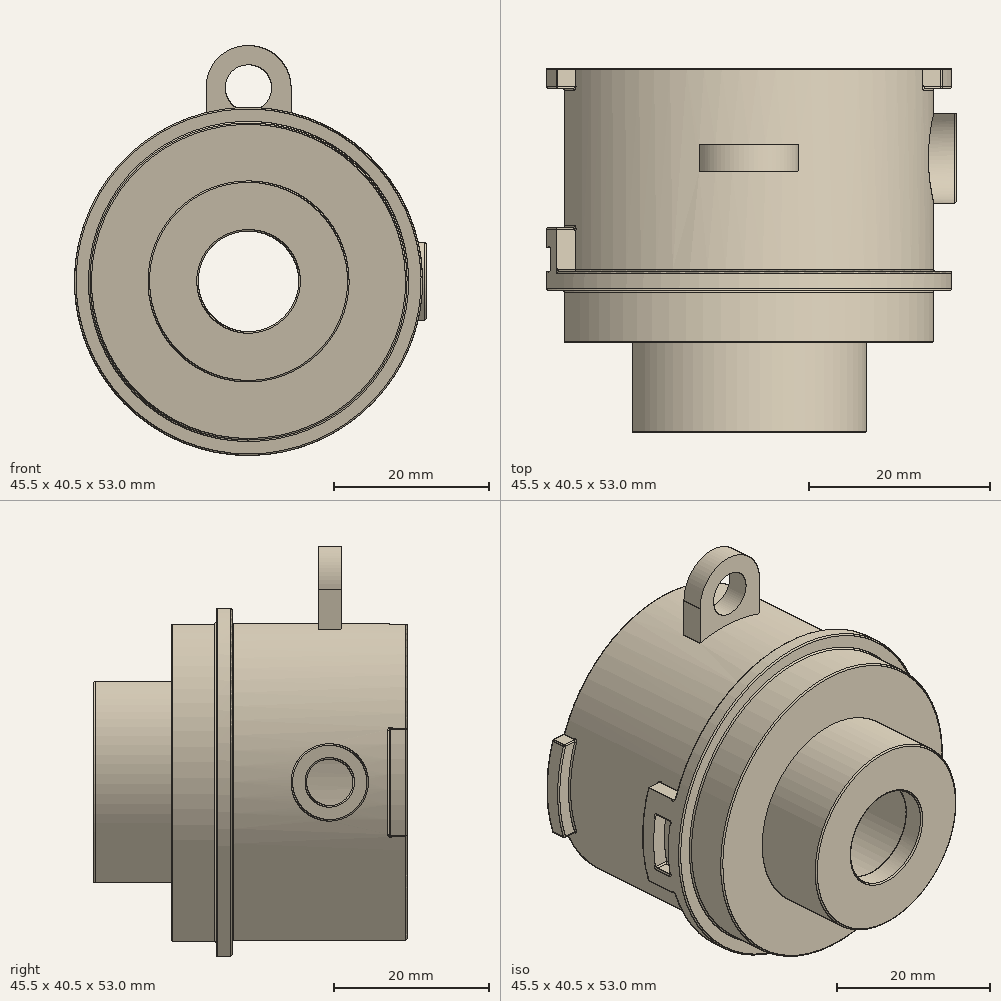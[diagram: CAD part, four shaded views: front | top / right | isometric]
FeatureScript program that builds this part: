
annotation { "Feature Type Name" : "Feature", "Feature Type Description" : "" }
export const myFeature = defineFeature(function(context is Context, id is Id, definition is map)
    precondition{}
    {
        {
            var Q0;
            Q0=qCreatedBy(makeId("Front.planeOp"),FACE);
            var sketch = newSketch(context, id + "F0", { "sketchPlane" : qUnion([Q0])});
            skCircle(sketch, "E0", {"center": v(0, 0) * mm, "radius": 18.45 * mm});
            skCircle(sketch, "E1", {"center": v(0, 0) * mm, "radius": 20.5 * mm});
            skLineSegment(sketch, "E2.bottom", {"start": v(-19.27, 7) * mm, "end": v(-21.38, 7) * mm});
            skLineSegment(sketch, "E3.MirrorCS", {"start": v(19.27, 7) * mm, "end": v(21.38, 7) * mm});
            skLineSegment(sketch, "E4.MirrorCS", {"start": v(-19.27, -7) * mm, "end": v(-21.38, -7) * mm});
            skLineSegment(sketch, "E5.MirrorCS", {"start": v(19.27, -7) * mm, "end": v(21.38, -7) * mm});
            skArc(sketch, "E6", {"start": v(21.38, -7) * mm, "mid": v(22.5, 0) * mm, "end": v(21.38, 7) * mm});
            skArc(sketch, "E7.trimOffspring", {"start": v(-21.38, 7) * mm, "mid": v(-22.5, 0) * mm, "end": v(-21.38, -7) * mm});
            skSolve(sketch);
        }
        {
            var Q0;
            Q0=makeQuery(id+"F0.imprint","IMPRINT",FACE,{"disambiguationData":[TD([[makeQuery(id+"F0.imprint","IMPRINT",EDGE,{"derivedFrom":sQuery(id+"F0.wireOp",EDGE,"E0")}),-1.0]])]});
            extrude(context, id + "F1", {"entities" : qUnion([Q0]), "depth" : 27.5 * mm});
        }
        {
            var Q0;
            {var subQ0=sQuery(id+"F0.wireOp",EDGE,"E2.bottom");Q0=makeQuery(id+"F0.imprint","IMPRINT",FACE,{"disambiguationData":[TD([[makeQuery(id+"F0.imprint","IMPRINT",EDGE,{"derivedFrom":subQ0}),1.0]])]});}
            var Q1;
            {var subQ0=sQuery(id+"F0.wireOp",EDGE,"E3.MirrorCS");Q1=makeQuery(id+"F0.imprint","IMPRINT",FACE,{"disambiguationData":[TD([[makeQuery(id+"F0.imprint","IMPRINT",EDGE,{"derivedFrom":subQ0}),-1.0]])]});}
            extrude(context, id + "F2", {"entities" : qUnion([Q0, Q1]), "operationType" : NewBodyOperationType.ADD, "depth" : 2.3 * mm});
        }
        {
            var Q0;
            Q0=qCreatedBy(makeId("Front.planeOp"),FACE);
            cPlane(context, id + "F3", {"entities" : qUnion([Q0]), "cplaneType" : CPlaneType.OFFSET, "offset" : 2.1 * mm, "width" : 150 * mm, "height" : 150 * mm});
        }
        {
            var Q0;
            Q0=qCreatedBy(id+"F3.planeOp",FACE);
            var sketch = newSketch(context, id + "F4", { "sketchPlane" : qUnion([Q0])});
            skCircle(sketch, "E8", {"center": v(0, 0) * mm, "radius": 19.5 * mm});
            skLineSegment(sketch, "E9", {"start": v(0, 0) * mm, "end": v(-19.34, 2.5) * mm});
            skLineSegment(sketch, "E10", {"start": v(0, 0) * mm, "end": v(-19.34, -2.5) * mm});
            skLineSegment(sketch, "E11", {"start": v(0, 0) * mm, "end": v(-17.3, -9) * mm});
            skSolve(sketch);
        }
        {
            var Q0;
            {var subQ0=sQuery(id+"F4.wireOp",EDGE,"E9");Q0=makeQuery(id+"F4.imprint","IMPRINT",FACE,{"disambiguationData":[TD([[makeQuery(id+"F4.imprint","IMPRINT",EDGE,{"derivedFrom":subQ0}),1.0]])]});}
            var Q1;
            {var subQ0=sQuery(id+"F4.wireOp",EDGE,"E10");Q1=makeQuery(id+"F4.imprint","IMPRINT",FACE,{"disambiguationData":[TD([[makeQuery(id+"F4.imprint","IMPRINT",EDGE,{"derivedFrom":subQ0}),1.0]])]});}
            extrude(context, id + "F5", {"entities" : qUnion([Q0, Q1]), "operationType" : NewBodyOperationType.REMOVE, "depth" : 1.8 * mm});
        }
        {
            var Q0;
            {var subQ0=sQuery(id+"F4.wireOp",EDGE,"E10");Q0=makeQuery(id+"F4.imprint","IMPRINT",FACE,{"disambiguationData":[TD([[makeQuery(id+"F4.imprint","IMPRINT",EDGE,{"derivedFrom":subQ0}),1.0]])]});}
            extrude(context, id + "F6", {"entities" : qUnion([Q0]), "operationType" : NewBodyOperationType.REMOVE, "oppositeDirection" : true, "depth" : 25 * mm});
        }
        {
            var Q0;
            Q0=qCreatedBy(makeId("Front.planeOp"),FACE);
            var sketch = newSketch(context, id + "F7", { "sketchPlane" : qUnion([Q0])});
            skLineSegment(sketch, "E12.bottom", {"start": v(-1.65, 19.45) * mm, "end": v(1.65, 19.45) * mm});
            skLineSegment(sketch, "E12.top", {"start": v(-1.65, -19.45) * mm, "end": v(1.65, -19.45) * mm});
            skLineSegment(sketch, "E12.left", {"start": v(-1.65, 19.45) * mm, "end": v(-1.65, -19.45) * mm});
            skLineSegment(sketch, "E12.right", {"start": v(1.65, 19.45) * mm, "end": v(1.65, -19.45) * mm});
            skSolve(sketch);
        }
        {
            var Q0;
            Q0=makeQuery(id+"F7.imprint","IMPRINT",FACE,{"disambiguationData":[TD([[makeQuery(id+"F7.imprint","IMPRINT",EDGE,{"derivedFrom":sQuery(id+"F7.wireOp",EDGE,"E12.bottom")}),-1.0]])]});
            extrude(context, id + "F8", {"entities" : qUnion([Q0]), "operationType" : NewBodyOperationType.REMOVE, "depth" : 6.4 * mm});
        }
        {
            var Q0;
            Q0=makeQuery(id+"F8.boolean.opBoolean","INTERSECT",EDGE,{"disambiguationData":[OD(0.0)],"derivedFrom":[makeQuery(id+"F1.opExtrude","SWEPT_FACE",FACE,{"disambiguationData":[OSD([sQuery(id+"F0.wireOp",EDGE,"E0")])]}),makeQuery(id+"F8.opExtrude","SWEPT_FACE",FACE,{"disambiguationData":[OSD([sQuery(id+"F7.wireOp",EDGE,"E12.left")])]})]});
            var Q1;
            Q1=makeQuery(id+"F8.boolean.opBoolean","INTERSECT",EDGE,{"disambiguationData":[OD(0.0)],"derivedFrom":[makeQuery(id+"F1.opExtrude","SWEPT_FACE",FACE,{"disambiguationData":[OSD([sQuery(id+"F0.wireOp",EDGE,"E0")])]}),makeQuery(id+"F8.opExtrude","SWEPT_FACE",FACE,{"disambiguationData":[OSD([sQuery(id+"F7.wireOp",EDGE,"E12.right")])]})]});
            var Q2;
            Q2=makeQuery(id+"F8.boolean.opBoolean","INTERSECT",EDGE,{"disambiguationData":[OD(1.0)],"derivedFrom":[makeQuery(id+"F1.opExtrude","SWEPT_FACE",FACE,{"disambiguationData":[OSD([sQuery(id+"F0.wireOp",EDGE,"E0")])]}),makeQuery(id+"F8.opExtrude","SWEPT_FACE",FACE,{"disambiguationData":[OSD([sQuery(id+"F7.wireOp",EDGE,"E12.left")])]})]});
            var Q3;
            Q3=makeQuery(id+"F8.boolean.opBoolean","INTERSECT",EDGE,{"disambiguationData":[OD(1.0)],"derivedFrom":[makeQuery(id+"F1.opExtrude","SWEPT_FACE",FACE,{"disambiguationData":[OSD([sQuery(id+"F0.wireOp",EDGE,"E0")])]}),makeQuery(id+"F8.opExtrude","SWEPT_FACE",FACE,{"disambiguationData":[OSD([sQuery(id+"F7.wireOp",EDGE,"E12.right")])]})]});
            chamfer(context, id + "F9", {"entities" : qUnion([Q0, Q1, Q2, Q3]), "width" : 1 * mm, "tangentPropagation" : true});
        }
        {
            var Q0;
            Q0=qCreatedBy(makeId("Front.planeOp"),FACE);
            cPlane(context, id + "F10", {"entities" : qUnion([Q0]), "cplaneType" : CPlaneType.OFFSET, "offset" : 22.6 * mm, "width" : 150 * mm, "height" : 150 * mm});
        }
        {
            var Q0;
            Q0=qCreatedBy(id+"F10.planeOp",FACE);
            var sketch = newSketch(context, id + "F11", { "sketchPlane" : qUnion([Q0])});
            skCircle(sketch, "E13", {"center": v(0, 0) * mm, "radius": 22.5 * mm});
            skArc(sketch, "E14.0.0", {"start": v(-19.27, -7) * mm, "mid": v(-20.5, 0) * mm, "end": v(-19.27, 7) * mm});
            skLineSegment(sketch, "E14.0.1", {"start": v(-19.27, 7) * mm, "end": v(-21.38, 7) * mm});
            skArc(sketch, "E14.0.2", {"start": v(-21.38, 7) * mm, "mid": v(-22.5, 0) * mm, "end": v(-21.38, -7) * mm});
            skLineSegment(sketch, "E14.0.3", {"start": v(-21.38, -7) * mm, "end": v(-19.27, -7) * mm});
            skLineSegment(sketch, "E15.0.0", {"start": v(21.38, 7) * mm, "end": v(19.27, 7) * mm});
            skArc(sketch, "E15.0.1", {"start": v(19.27, 7) * mm, "mid": v(20.5, 0) * mm, "end": v(19.27, -7) * mm});
            skLineSegment(sketch, "E15.0.2", {"start": v(19.27, -7) * mm, "end": v(21.38, -7) * mm});
            skArc(sketch, "E15.0.3", {"start": v(21.38, -7) * mm, "mid": v(22.5, 0) * mm, "end": v(21.38, 7) * mm});
            skLineSegment(sketch, "E16", {"start": v(-20.1, 4) * mm, "end": v(-22.14, 4) * mm});
            skLineSegment(sketch, "E17", {"start": v(-20.1, -4) * mm, "end": v(-22.14, -4) * mm});
            skCircle(sketch, "E18", {"center": v(0, 0) * mm, "radius": 20.5 * mm});
            skSolve(sketch);
        }
        {
            var Q0;
            {var subQ0=sQuery(id+"F11.wireOp",EDGE,"E14.0.1");Q0=makeQuery(id+"F11.imprint","IMPRINT",FACE,{"disambiguationData":[TD([[makeQuery(id+"F11.imprint","IMPRINT",EDGE,{"derivedFrom":subQ0}),1.0]])]});}
            var Q1;
            {var subQ0=sQuery(id+"F11.wireOp",EDGE,"E16");Q1=makeQuery(id+"F11.imprint","IMPRINT",FACE,{"disambiguationData":[TD([[makeQuery(id+"F11.imprint","IMPRINT",EDGE,{"derivedFrom":subQ0}),1.0]])]});}
            var Q2;
            {var subQ0=sQuery(id+"F11.wireOp",EDGE,"E14.0.3");Q2=makeQuery(id+"F11.imprint","IMPRINT",FACE,{"disambiguationData":[TD([[makeQuery(id+"F11.imprint","IMPRINT",EDGE,{"derivedFrom":subQ0}),1.0]])]});}
            extrude(context, id + "F12", {"entities" : qUnion([Q0, Q1, Q2]), "operationType" : NewBodyOperationType.ADD, "oppositeDirection" : true, "depth" : 4.9 * mm, "hasSecondDirection" : true, "secondDirectionOppositeDirection" : false, "secondDirectionDepth" : 2.1 * mm});
        }
        {
            var Q0;
            {var subQ0=sQuery(id+"F11.wireOp",EDGE,"E16");Q0=makeQuery(id+"F11.imprint","IMPRINT",FACE,{"disambiguationData":[TD([[makeQuery(id+"F11.imprint","IMPRINT",EDGE,{"derivedFrom":subQ0}),1.0]])]});}
            extrude(context, id + "F13", {"entities" : qUnion([Q0]), "operationType" : NewBodyOperationType.REMOVE, "oppositeDirection" : true, "depth" : 2.7 * mm});
        }
        {
            var Q0;
            {var subQ0=sQuery(id+"F11.wireOp",EDGE,"E14.0.3");Q0=makeQuery(id+"F11.imprint","IMPRINT",FACE,{"disambiguationData":[TD([[makeQuery(id+"F11.imprint","IMPRINT",EDGE,{"derivedFrom":subQ0}),-1.0]])]});}
            var Q1;
            {var subQ0=sQuery(id+"F11.wireOp",EDGE,"E14.0.1");Q1=makeQuery(id+"F11.imprint","IMPRINT",FACE,{"disambiguationData":[TD([[makeQuery(id+"F11.imprint","IMPRINT",EDGE,{"derivedFrom":subQ0}),-1.0]])]});}
            var Q2;
            {var subQ0=sQuery(id+"F11.wireOp",EDGE,"E15.0.0");Q2=makeQuery(id+"F11.imprint","IMPRINT",FACE,{"disambiguationData":[TD([[makeQuery(id+"F11.imprint","IMPRINT",EDGE,{"derivedFrom":subQ0}),1.0]])]});}
            extrude(context, id + "F14", {"entities" : qUnion([Q0, Q1, Q2]), "operationType" : NewBodyOperationType.ADD, "depth" : 2.1 * mm});
        }
        {
            var Q0;
            Q0=makeQuery(id+"F13.boolean.opBoolean","COPY",FACE,{"derivedFrom":makeQuery(id+"F13.opExtrude","SWEPT_FACE",FACE,{"disambiguationData":[OSD([sQuery(id+"F11.wireOp",EDGE,"E16")])]})});
            var Q1;
            Q1=makeQuery(id+"F13.boolean.opBoolean","COPY",FACE,{"derivedFrom":makeQuery(id+"F13.opExtrude","SWEPT_FACE",FACE,{"disambiguationData":[OSD([sQuery(id+"F11.wireOp",EDGE,"E17")])]})});
            var Q2;
            Q2=makeQuery(id+"F12.opExtrude","CAP_FACE",FACE,{"disambiguationData":[OSD([sQuery(id+"F11.wireOp",EDGE,"E13"),sQuery(id+"F11.wireOp",EDGE,"E14.0.1"),sQuery(id+"F11.wireOp",EDGE,"E14.0.3"),sQuery(id+"F11.wireOp",EDGE,"E18")])],"isStart":false});
            var Q3;
            {var subQ0=sQuery(id+"F11.wireOp",EDGE,"E13");var subQ1=sQuery(id+"F11.wireOp",EDGE,"E14.0.3");var subQ2=sQuery(id+"F11.wireOp",EDGE,"E14.0.1");Q3=makeQuery(id+"F14.boolean.opBoolean","SPLIT",FACE,{"disambiguationData":[TD([makeQuery(id+"F12.opExtrude","SWEPT_FACE",FACE,{"disambiguationData":[OSD([subQ1])]})])],"derivedFrom":makeQuery(id+"F14.opExtrude","CAP_FACE",FACE,{"disambiguationData":[OSD([subQ0,subQ2,subQ1,sQuery(id+"F11.wireOp",EDGE,"E18")])],"isStart":true})});}
            var Q4;
            {var subQ0=sQuery(id+"F11.wireOp",EDGE,"E13");var subQ1=sQuery(id+"F11.wireOp",EDGE,"E14.0.1");var subQ2=sQuery(id+"F11.wireOp",EDGE,"E14.0.3");Q4=makeQuery(id+"F14.boolean.opBoolean","SPLIT",FACE,{"disambiguationData":[TD([makeQuery(id+"F12.opExtrude","SWEPT_FACE",FACE,{"disambiguationData":[OSD([subQ1])]})])],"derivedFrom":makeQuery(id+"F14.opExtrude","CAP_FACE",FACE,{"disambiguationData":[OSD([subQ0,subQ1,subQ2,sQuery(id+"F11.wireOp",EDGE,"E18")])],"isStart":true})});}
            var Q5;
            Q5=makeQuery(id+"FDiJdH3o1XdmGiN_1.1.F12.opExtrude","CAP_FACE",FACE,{"disambiguationData":[OSD([sQuery(id+"F11.wireOp",EDGE,"E13"),sQuery(id+"F11.wireOp",EDGE,"E14.0.1"),sQuery(id+"F11.wireOp",EDGE,"E14.0.3"),sQuery(id+"F11.wireOp",EDGE,"E18")])],"isStart":false});
            var Q6;
            Q6=makeQuery(id+"FDiJdH3o1XdmGiN_1.1.F13.boolean.opBoolean","COPY",FACE,{"derivedFrom":makeQuery(id+"FDiJdH3o1XdmGiN_1.1.F13.opExtrude","SWEPT_FACE",FACE,{"disambiguationData":[OSD([sQuery(id+"F11.wireOp",EDGE,"E17")])]})});
            var Q7;
            Q7=makeQuery(id+"FDiJdH3o1XdmGiN_1.1.F13.boolean.opBoolean","COPY",FACE,{"derivedFrom":makeQuery(id+"FDiJdH3o1XdmGiN_1.1.F13.opExtrude","SWEPT_FACE",FACE,{"disambiguationData":[OSD([sQuery(id+"F11.wireOp",EDGE,"E16")])]})});
            fillet(context, id + "F15", {"entities" : qUnion([Q0, Q1, Q2, Q3, Q4, Q5, Q6, Q7]), "radius" : 0.2 * mm, "tangentPropagation" : true, "allowEdgeOverflow" : false});
        }
        {
            var Q0;
            {var subQ0=sQuery(id+"F11.wireOp",EDGE,"E18");var subQ1=sQuery(id+"F11.wireOp",EDGE,"E14.0.3");var subQ2=sQuery(id+"F11.wireOp",EDGE,"E14.0.1");var subQ3=sQuery(id+"F11.wireOp",EDGE,"E13");Q0=makeQuery(id+"F14.boolean.opBoolean","MERGE",FACE,{"derivedFrom":[makeQuery(id+"F12.opExtrude","CAP_FACE",FACE,{"disambiguationData":[OSD([subQ3,subQ2,subQ1,subQ0])],"isStart":true}),makeQuery(id+"FDiJdH3o1XdmGiN_1.1.F12.opExtrude","CAP_FACE",FACE,{"disambiguationData":[OSD([subQ3,subQ2,subQ1,subQ0])],"isStart":true}),makeQuery(id+"F14.opExtrude","CAP_FACE",FACE,{"disambiguationData":[OSD([subQ3,subQ2,subQ1,subQ0])],"isStart":false})]});}
            var Q1;
            Q1=makeQuery(id+"F2.opExtrude","CAP_FACE",FACE,{"disambiguationData":[OSD([sQuery(id+"F0.wireOp",EDGE,"E1"),sQuery(id+"F0.wireOp",EDGE,"E2.bottom"),sQuery(id+"F0.wireOp",EDGE,"E4.MirrorCS"),sQuery(id+"F0.wireOp",EDGE,"E7.trimOffspring")])],"isStart":false});
            var Q2;
            Q2=makeQuery(id+"F2.opExtrude","CAP_FACE",FACE,{"disambiguationData":[OSD([sQuery(id+"F0.wireOp",EDGE,"E1"),sQuery(id+"F0.wireOp",EDGE,"E3.MirrorCS"),sQuery(id+"F0.wireOp",EDGE,"E5.MirrorCS"),sQuery(id+"F0.wireOp",EDGE,"E6")])],"isStart":false});
            var Q3;
            {var subQ0=sQuery(id+"F0.wireOp",EDGE,"E1");Q3=makeQuery(id+"F2.boolean.opBoolean","MERGE",FACE,{"derivedFrom":[makeQuery(id+"F1.opExtrude","CAP_FACE",FACE,{"disambiguationData":[OSD([sQuery(id+"F0.wireOp",EDGE,"E0"),subQ0])],"isStart":true}),makeQuery(id+"F2.opExtrude","CAP_FACE",FACE,{"disambiguationData":[OSD([subQ0,sQuery(id+"F0.wireOp",EDGE,"E2.bottom"),sQuery(id+"F0.wireOp",EDGE,"E4.MirrorCS"),sQuery(id+"F0.wireOp",EDGE,"E7.trimOffspring")])],"isStart":true}),makeQuery(id+"F2.opExtrude","CAP_FACE",FACE,{"disambiguationData":[OSD([subQ0,sQuery(id+"F0.wireOp",EDGE,"E3.MirrorCS"),sQuery(id+"F0.wireOp",EDGE,"E5.MirrorCS"),sQuery(id+"F0.wireOp",EDGE,"E6")])],"isStart":true})]});}
            var Q4;
            Q4=makeQuery(id+"F2.opExtrude","SWEPT_FACE",FACE,{"disambiguationData":[OSD([sQuery(id+"F0.wireOp",EDGE,"E6")])]});
            var Q5;
            Q5=makeQuery(id+"F2.opExtrude","SWEPT_FACE",FACE,{"disambiguationData":[OSD([sQuery(id+"F0.wireOp",EDGE,"E7.trimOffspring")])]});
            fillet(context, id + "F16", {"entities" : qUnion([Q0, Q1, Q2, Q3, Q4, Q5]), "radius" : 0.2 * mm, "tangentPropagation" : true, "allowEdgeOverflow" : false});
        }
        {
            var Q0;
            Q0=makeQuery(id+"F1.opExtrude","CAP_FACE",FACE,{"disambiguationData":[OSD([sQuery(id+"F0.wireOp",EDGE,"E0"),sQuery(id+"F0.wireOp",EDGE,"E1")])],"isStart":false});
            var sketch = newSketch(context, id + "F17", { "sketchPlane" : qUnion([Q0])});
            skCircle(sketch, "E19.0", {"center": v(0, 0) * mm, "radius": 18.45 * mm});
            skCircle(sketch, "E20", {"center": v(0, 0) * mm, "radius": 9 * mm});
            skSolve(sketch);
        }
        {
            var Q0;
            Q0=makeQuery(id+"F17.imprint","IMPRINT",FACE,{"disambiguationData":[TD([[makeQuery(id+"F17.imprint","IMPRINT",EDGE,{"derivedFrom":sQuery(id+"F17.wireOp",EDGE,"E19.0")}),1.0]])]});
            var Q1;
            Q1=makeQuery(id+"F17.imprint","IMPRINT",FACE,{"disambiguationData":[TD([[makeQuery(id+"F17.imprint","IMPRINT",EDGE,{"derivedFrom":sQuery(id+"F17.wireOp",EDGE,"E19.0")}),-1.0]])]});
            extrude(context, id + "F18", {"entities" : qUnion([Q0, Q1]), "operationType" : NewBodyOperationType.ADD, "depth" : 3 * mm});
        }
        {
            var Q0;
            Q0=qCreatedBy(makeId("Top.planeOp"),FACE);
            var sketch = newSketch(context, id + "F19", { "sketchPlane" : qUnion([Q0])});
            skLineSegment(sketch, "E21", {"start": v(13, -40.5) * mm, "end": v(13, -30.5) * mm});
            skLineSegment(sketch, "E22", {"start": v(13, -30.5) * mm, "end": v(9, -30.5) * mm});
            skLineSegment(sketch, "E23.top", {"start": v(9, -37.5) * mm, "end": v(6.5, -37.5) * mm});
            skLineSegment(sketch, "E23.right", {"start": v(6.5, -40.5) * mm, "end": v(6.5, -37.5) * mm});
            skLineSegment(sketch, "E24", {"start": v(9, -30.5) * mm, "end": v(9, -37.5) * mm});
            skLineSegment(sketch, "E25", {"start": v(6.5, -40.5) * mm, "end": v(13, -40.5) * mm});
            skLineSegment(sketch, "E26", {"start": v(0, 0) * mm, "end": v(0, -50) * mm, "construction": true});
            skSolve(sketch);
        }
        {
            var Q0;
            Q0=makeQuery(id+"F19.imprint","IMPRINT",FACE,{"disambiguationData":[TD([[makeQuery(id+"F19.imprint","IMPRINT",EDGE,{"derivedFrom":sQuery(id+"F19.wireOp",EDGE,"E21")}),1.0]])]});
            var Q1;
            Q1=sQuery(id+"F19.wireOp",EDGE,"E26");
            revolve(context, id + "F20", {"operationType" : NewBodyOperationType.ADD, "entities" : qUnion([Q0]), "axis" : qUnion([Q1]), "revolveType" : RevolveType.FULL});
        }
        {
            var Q0;
            Q0=makeQuery(id+"F18.opExtrude","CAP_EDGE",EDGE,{"disambiguationData":[OSD([sQuery(id+"F0.wireOp",EDGE,"E1")])],"isStart":false});
            var Q1;
            Q1=makeQuery(id+"F1.opExtrude","CAP_EDGE",EDGE,{"disambiguationData":[OSD([sQuery(id+"F0.wireOp",EDGE,"E0")])],"isStart":false});
            var Q2;
            Q2=makeQuery(id+"F20.opRevolve","SWEPT_EDGE",EDGE,{"disambiguationData":[OSD([sQuery(id+"F19.wireOp",EDGE,"TMA1aJ2l-3Chm-zUbr-5o9L-zpnb6GAkEytc"),sQuery(id+"F19.wireOp",EDGE,"E21")])]});
            var Q3;
            Q3=makeQuery(id+"F20.opRevolve","SWEPT_EDGE",EDGE,{"disambiguationData":[OSD([sQuery(id+"F19.wireOp",EDGE,"E23.bottom"),sQuery(id+"F19.wireOp",EDGE,"E23.right")])]});
            var Q4;
            Q4=makeQuery(id+"F20.opRevolve","SWEPT_FACE",FACE,{"disambiguationData":[OSD([sQuery(id+"F19.wireOp",EDGE,"E23.top")])]});
            var Q5;
            Q5=makeQuery(id+"F18.opExtrude","CAP_EDGE",EDGE,{"disambiguationData":[OSD([sQuery(id+"F17.wireOp",EDGE,"E20")])],"isStart":true});
            fillet(context, id + "F21", {"entities" : qUnion([Q0, Q1, Q2, Q3, Q4, Q5]), "radius" : 0.2 * mm, "tangentPropagation" : true, "allowEdgeOverflow" : false});
        }
        {
            var Q0;
            Q0=qCreatedBy(makeId("Front.planeOp"),FACE);
            cPlane(context, id + "F22", {"entities" : qUnion([Q0]), "cplaneType" : CPlaneType.OFFSET, "offset" : 10 * mm, "width" : 150 * mm, "height" : 150 * mm});
        }
        {
            var Q0;
            Q0=qCreatedBy(id+"F22.planeOp",FACE);
            var sketch = newSketch(context, id + "F23", { "sketchPlane" : qUnion([Q0])});
            skCircle(sketch, "E27", {"center": v(0, 25) * mm, "radius": 3 * mm});
            skArc(sketch, "E28", {"start": v(5.5, 25) * mm, "mid": v(0, 30.5) * mm, "end": v(-5.5, 25) * mm});
            skLineSegment(sketch, "E29", {"start": v(5.5, 25) * mm, "end": v(5.5, 19) * mm});
            skLineSegment(sketch, "E30", {"start": v(5.5, 19) * mm, "end": v(-5.5, 19) * mm});
            skLineSegment(sketch, "E31", {"start": v(-5.5, 19) * mm, "end": v(-5.5, 25) * mm});
            skSolve(sketch);
        }
        {
            var Q0;
            Q0 = qSketchRegion(id + "F23", true);
            extrude(context, id + "F24", {"entities" : qUnion([Q0]), "operationType" : NewBodyOperationType.ADD, "endBound" : BoundingType.SYMMETRIC, "depth" : 3 * mm});
        }
        {
            var Q0;
            Q0=qCreatedBy(makeId("Right.planeOp"),FACE);
            cPlane(context, id + "F25", {"entities" : qUnion([Q0]), "cplaneType" : CPlaneType.OFFSET, "offset" : 23 * mm, "width" : 150 * mm, "height" : 150 * mm});
        }
        {
            var Q0;
            Q0=qCreatedBy(id+"F25.planeOp",FACE);
            var sketch = newSketch(context, id + "F26", { "sketchPlane" : qUnion([Q0])});
            skCircle(sketch, "E32", {"center": v(-10, 0) * mm, "radius": 3 * mm});
            skCircle(sketch, "E33", {"center": v(-10, 0) * mm, "radius": 5 * mm});
            skSolve(sketch);
        }
        {
            var Q0;
            Q0=makeQuery(id+"F26.imprint","IMPRINT",FACE,{"disambiguationData":[TD([[makeQuery(id+"F26.imprint","IMPRINT",EDGE,{"derivedFrom":sQuery(id+"F26.wireOp",EDGE,"E32")}),1.0]])]});
            var Q1;
            Q1=makeQuery(id+"F1.opExtrude","SWEPT_FACE",FACE,{"disambiguationData":[OSD([sQuery(id+"F0.wireOp",EDGE,"E0")])]});
            extrude(context, id + "F27", {"entities" : qUnion([Q0]), "operationType" : NewBodyOperationType.REMOVE, "endBound" : BoundingType.UP_TO_SURFACE, "oppositeDirection" : true, "endBoundEntityFace" : qUnion([Q1]), "depth" : 50 * mm});
        }
        {
            var Q0;
            Q0=makeQuery(id+"F26.imprint","IMPRINT",FACE,{"disambiguationData":[TD([[makeQuery(id+"F26.imprint","IMPRINT",EDGE,{"derivedFrom":sQuery(id+"F26.wireOp",EDGE,"E32")}),-1.0]])]});
            extrude(context, id + "F28", {"entities" : qUnion([Q0]), "operationType" : NewBodyOperationType.ADD, "endBound" : BoundingType.UP_TO_NEXT, "oppositeDirection" : true, "depth" : 25 * mm});
        }
        {
            var Q0;
            Q0=makeQuery(id+"F24.opExtrude","CAP_FACE",FACE,{"disambiguationData":[OSD([sQuery(id+"F23.wireOp",EDGE,"GQkDEcLr-gr8e-p2JM-y6pI-lHilVU4eMQgI"),sQuery(id+"F23.wireOp",EDGE,"qEbbBfWA-n2UN-SD92-FDw2-pZqtjRNXadgX"),sQuery(id+"F23.wireOp",EDGE,"8QATue7S-7j6Q-Mm7R-N72I-EgzRiDab2Tbp"),sQuery(id+"F23.wireOp",EDGE,"DwYRGvjy-Wigq-bkY5-MHbX-W4qbPHjbdQl9"),sQuery(id+"F23.wireOp",EDGE,"JhXbNAtQ-5Quj-yZyU-fEKm-X3ZlWfEUQUUQ")])],"isStart":true});
            var Q1;
            Q1=makeQuery(id+"F24.opExtrude","CAP_FACE",FACE,{"disambiguationData":[OSD([sQuery(id+"F23.wireOp",EDGE,"GQkDEcLr-gr8e-p2JM-y6pI-lHilVU4eMQgI"),sQuery(id+"F23.wireOp",EDGE,"qEbbBfWA-n2UN-SD92-FDw2-pZqtjRNXadgX"),sQuery(id+"F23.wireOp",EDGE,"8QATue7S-7j6Q-Mm7R-N72I-EgzRiDab2Tbp"),sQuery(id+"F23.wireOp",EDGE,"DwYRGvjy-Wigq-bkY5-MHbX-W4qbPHjbdQl9"),sQuery(id+"F23.wireOp",EDGE,"JhXbNAtQ-5Quj-yZyU-fEKm-X3ZlWfEUQUUQ")])],"isStart":false});
            var Q2;
            Q2=makeQuery(id+"F28.opExtrude","CAP_FACE",FACE,{"disambiguationData":[OSD([sQuery(id+"F26.wireOp",EDGE,"E32"),sQuery(id+"F26.wireOp",EDGE,"E33")])],"isStart":true});
            var Q3;
            {var subQ7=sQuery(id+"F0.wireOp",EDGE,"E1");var subQ8=sQuery(id+"F0.wireOp",EDGE,"E2.bottom");Q3=makeQuery(id+"F28.opExtrude","TWEAK_EDGE",EDGE,{"derivedFrom":[makeQuery(id+"F26.imprint","IMPRINT",EDGE,{"derivedFrom":sQuery(id+"F26.wireOp",EDGE,"E33")}),makeQuery(id+"F14.boolean.opBoolean","SPLIT",FACE,{"disambiguationData":[TD([makeQuery(id+"F2.opExtrude","SWEPT_FACE",FACE,{"disambiguationData":[OSD([subQ8])]})])],"derivedFrom":makeQuery(id+"F1.opExtrude","SWEPT_FACE",FACE,{"disambiguationData":[OSD([subQ7])]})})]});}
            var Q4;
            {var subQ7=sQuery(id+"F0.wireOp",EDGE,"E1");var subQ8=sQuery(id+"F0.wireOp",EDGE,"E2.bottom");Q4=makeQuery(id+"Fni3u0OuxvgQHvp_1.1.F28.opExtrude","TWEAK_EDGE",EDGE,{"derivedFrom":[makeQuery(id+"F26.imprint","IMPRINT",EDGE,{"derivedFrom":sQuery(id+"F26.wireOp",EDGE,"E33")}),makeQuery(id+"F14.boolean.opBoolean","SPLIT",FACE,{"disambiguationData":[TD([makeQuery(id+"F2.opExtrude","SWEPT_FACE",FACE,{"disambiguationData":[OSD([subQ8])]})])],"derivedFrom":makeQuery(id+"F1.opExtrude","SWEPT_FACE",FACE,{"disambiguationData":[OSD([subQ7])]})})]});}
            var Q5;
            Q5=makeQuery(id+"Fni3u0OuxvgQHvp_1.1.F28.opExtrude","CAP_EDGE",EDGE,{"disambiguationData":[OSD([sQuery(id+"F26.wireOp",EDGE,"E33")])],"isStart":true});
            fillet(context, id + "F29", {"entities" : qUnion([Q0, Q1, Q2, Q3, Q4, Q5]), "radius" : 0.2 * mm, "tangentPropagation" : true, "allowEdgeOverflow" : false});
        }
    });
